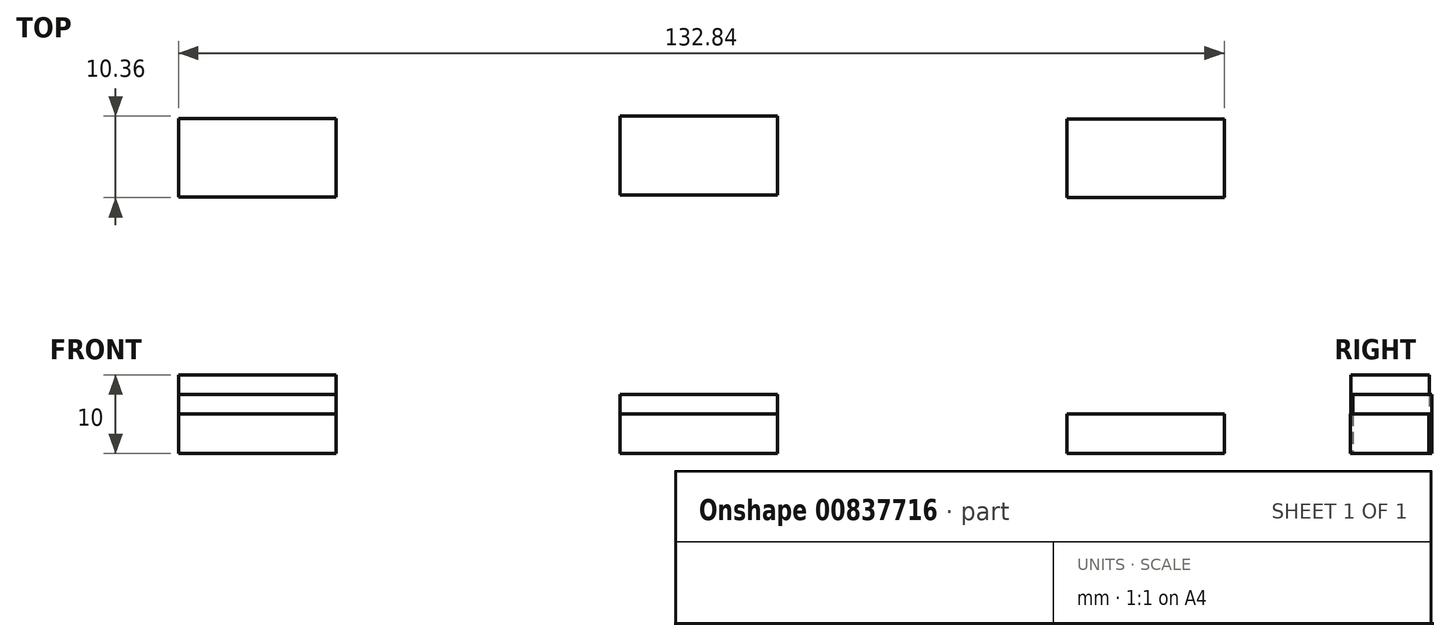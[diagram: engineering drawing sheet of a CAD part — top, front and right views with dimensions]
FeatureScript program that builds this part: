
annotation { "Feature Type Name" : "Feature", "Feature Type Description" : "" }
export const myFeature = defineFeature(function(context is Context, id is Id, definition is map)
    precondition{}
    {
        {
            var Q0;
            Q0=qCreatedBy(makeId("Top.planeOp"),FACE);
            var sketch = newSketch(context, id + "F0", { "sketchPlane" : qUnion([Q0])});
            skLineSegment(sketch, "E0.bottom", {"start": v(-66.09, 4.7) * mm, "end": v(-46.09, 4.7) * mm});
            skLineSegment(sketch, "E0.top", {"start": v(-66.09, -5.3) * mm, "end": v(-46.09, -5.3) * mm});
            skLineSegment(sketch, "E0.left", {"start": v(-66.09, 4.7) * mm, "end": v(-66.09, -5.3) * mm});
            skLineSegment(sketch, "E0.right", {"start": v(-46.09, 4.7) * mm, "end": v(-46.09, -5.3) * mm});
            skSolve(sketch);
        }
        {
            var Q0;
            Q0=makeQuery(id+"F0.imprint","IMPRINT",FACE,{"disambiguationData":[TD([[makeQuery(id+"F0.imprint","IMPRINT",EDGE,{"derivedFrom":sQuery(id+"F0.wireOp",EDGE,"E0.bottom")}),-1.0]])]});
            extrude(context, id + "F1", {"entities" : qUnion([Q0]), "depth" : 5 * mm, "offsetDistance" : 25 * mm});
        }
        {
            var Q0;
            Q0=qCreatedBy(makeId("Top.planeOp"),FACE);
            var sketch = newSketch(context, id + "F2", { "sketchPlane" : qUnion([Q0])});
            skLineSegment(sketch, "E1.bottom", {"start": v(46.75, 4.64) * mm, "end": v(66.75, 4.64) * mm});
            skLineSegment(sketch, "E1.top", {"start": v(46.75, -5.36) * mm, "end": v(66.75, -5.36) * mm});
            skLineSegment(sketch, "E1.left", {"start": v(46.75, 4.64) * mm, "end": v(46.75, -5.36) * mm});
            skLineSegment(sketch, "E1.right", {"start": v(66.75, 4.64) * mm, "end": v(66.75, -5.36) * mm});
            skSolve(sketch);
        }
        {
            var Q0;
            Q0=makeQuery(id+"F2.imprint","IMPRINT",FACE,{"disambiguationData":[TD([[makeQuery(id+"F2.imprint","IMPRINT",EDGE,{"derivedFrom":sQuery(id+"F2.wireOp",EDGE,"E1.bottom")}),-1.0]])]});
            extrude(context, id + "F3", {"entities" : qUnion([Q0]), "depth" : 5 * mm, "offsetDistance" : 25 * mm});
        }
        {
            var Q0;
            Q0=makeQuery(id+"F1.opExtrude","CAP_FACE",FACE,{"disambiguationData":[OSD([sQuery(id+"F0.wireOp",EDGE,"E0.bottom"),sQuery(id+"F0.wireOp",EDGE,"E0.top"),sQuery(id+"F0.wireOp",EDGE,"E0.left"),sQuery(id+"F0.wireOp",EDGE,"E0.right")])],"isStart":false});
            var sketch = newSketch(context, id + "F4", { "sketchPlane" : qUnion([Q0])});
            skLineSegment(sketch, "E2.bottom", {"start": v(-66.09, 4.7) * mm, "end": v(-46.09, 4.7) * mm});
            skLineSegment(sketch, "E2.top", {"start": v(-66.09, -5.3) * mm, "end": v(-46.09, -5.3) * mm});
            skLineSegment(sketch, "E2.left", {"start": v(-66.09, 4.7) * mm, "end": v(-66.09, -5.3) * mm});
            skLineSegment(sketch, "E2.right", {"start": v(-46.09, 4.7) * mm, "end": v(-46.09, -5.3) * mm});
            skSolve(sketch);
        }
        {
            var Q0;
            Q0 = qSketchRegion(id + "F4", true);
            extrude(context, id + "F5", {"entities" : qUnion([Q0]), "depth" : 2.5 * mm, "offsetDistance" : 25 * mm});
        }
        {
            var Q0;
            Q0=makeQuery(id+"F5.opExtrude","CAP_FACE",FACE,{"disambiguationData":[OSD([sQuery(id+"F4.wireOp",EDGE,"E2.bottom"),sQuery(id+"F4.wireOp",EDGE,"E2.top"),sQuery(id+"F4.wireOp",EDGE,"E2.left"),sQuery(id+"F4.wireOp",EDGE,"E2.right")])],"isStart":false});
            var sketch = newSketch(context, id + "F6", { "sketchPlane" : qUnion([Q0])});
            skLineSegment(sketch, "E3.bottom", {"start": v(-66.09, 4.7) * mm, "end": v(-46.09, 4.7) * mm});
            skLineSegment(sketch, "E3.top", {"start": v(-66.09, -5.3) * mm, "end": v(-46.09, -5.3) * mm});
            skLineSegment(sketch, "E3.left", {"start": v(-66.09, 4.7) * mm, "end": v(-66.09, -5.3) * mm});
            skLineSegment(sketch, "E3.right", {"start": v(-46.09, 4.7) * mm, "end": v(-46.09, -5.3) * mm});
            skSolve(sketch);
        }
        {
            var Q0;
            Q0 = qSketchRegion(id + "F6", true);
            extrude(context, id + "F7", {"entities" : qUnion([Q0]), "depth" : 2.5 * mm, "offsetDistance" : 25 * mm});
        }
        {
            var Q0;
            Q0=makeQuery(id+"F3.opExtrude","SWEPT_BODY",BODY,{"disambiguationData":[OSD([sQuery(id+"F2.wireOp",EDGE,"E1.bottom"),sQuery(id+"F2.wireOp",EDGE,"E1.top"),sQuery(id+"F2.wireOp",EDGE,"E1.left"),sQuery(id+"F2.wireOp",EDGE,"E1.right")])]});
            transform(context, id + "F8", {"entities" : qUnion([Q0]), "transformType" : TransformType.TRANSLATION_3D, "dx" : 5 * mm, "dy" : 5 * mm, "dz" : 5 * mm, "makeCopy" : true});
        }
        {
            var Q0;
            Q0=makeQuery(id+"F8.opPattern","COPY",BODY,{"derivedFrom":makeQuery(id+"F3.opExtrude","SWEPT_BODY",BODY,{"disambiguationData":[OSD([sQuery(id+"F2.wireOp",EDGE,"E1.bottom"),sQuery(id+"F2.wireOp",EDGE,"E1.top"),sQuery(id+"F2.wireOp",EDGE,"E1.left"),sQuery(id+"F2.wireOp",EDGE,"E1.right")])]}),"instanceName":"1"});
            deleteBodies(context, id + "F9", {"entities" : qUnion([Q0])});
        }
        {
            var Q0;
            Q0=qCreatedBy(makeId("Top.planeOp"),FACE);
            var sketch = newSketch(context, id + "F10", { "sketchPlane" : qUnion([Q0])});
            skLineSegment(sketch, "E4.bottom", {"start": v(-10, 5) * mm, "end": v(10, 5) * mm});
            skLineSegment(sketch, "E4.top", {"start": v(-10, -5) * mm, "end": v(10, -5) * mm});
            skLineSegment(sketch, "E4.left", {"start": v(-10, 5) * mm, "end": v(-10, -5) * mm});
            skLineSegment(sketch, "E4.right", {"start": v(10, 5) * mm, "end": v(10, -5) * mm});
            skSolve(sketch);
        }
        {
            var Q0;
            Q0 = qSketchRegion(id + "F10", true);
            extrude(context, id + "F11", {"entities" : qUnion([Q0]), "depth" : 5 * mm, "offsetDistance" : 25 * mm});
        }
        {
            var Q0;
            Q0=makeQuery(id+"F11.opExtrude","CAP_FACE",FACE,{"disambiguationData":[OSD([sQuery(id+"F10.wireOp",EDGE,"E4.bottom"),sQuery(id+"F10.wireOp",EDGE,"E4.top"),sQuery(id+"F10.wireOp",EDGE,"E4.left"),sQuery(id+"F10.wireOp",EDGE,"E4.right")])],"isStart":false});
            var sketch = newSketch(context, id + "F12", { "sketchPlane" : qUnion([Q0])});
            skLineSegment(sketch, "E5.bottom", {"start": v(-10, 5) * mm, "end": v(10, 5) * mm});
            skLineSegment(sketch, "E5.top", {"start": v(-10, -5) * mm, "end": v(10, -5) * mm});
            skLineSegment(sketch, "E5.left", {"start": v(-10, 5) * mm, "end": v(-10, -5) * mm});
            skLineSegment(sketch, "E5.right", {"start": v(10, 5) * mm, "end": v(10, -5) * mm});
            skSolve(sketch);
        }
        {
            var Q0;
            Q0 = qSketchRegion(id + "F12", true);
            extrude(context, id + "F13", {"entities" : qUnion([Q0]), "depth" : 2.5 * mm, "offsetDistance" : 25 * mm});
        }
    });
